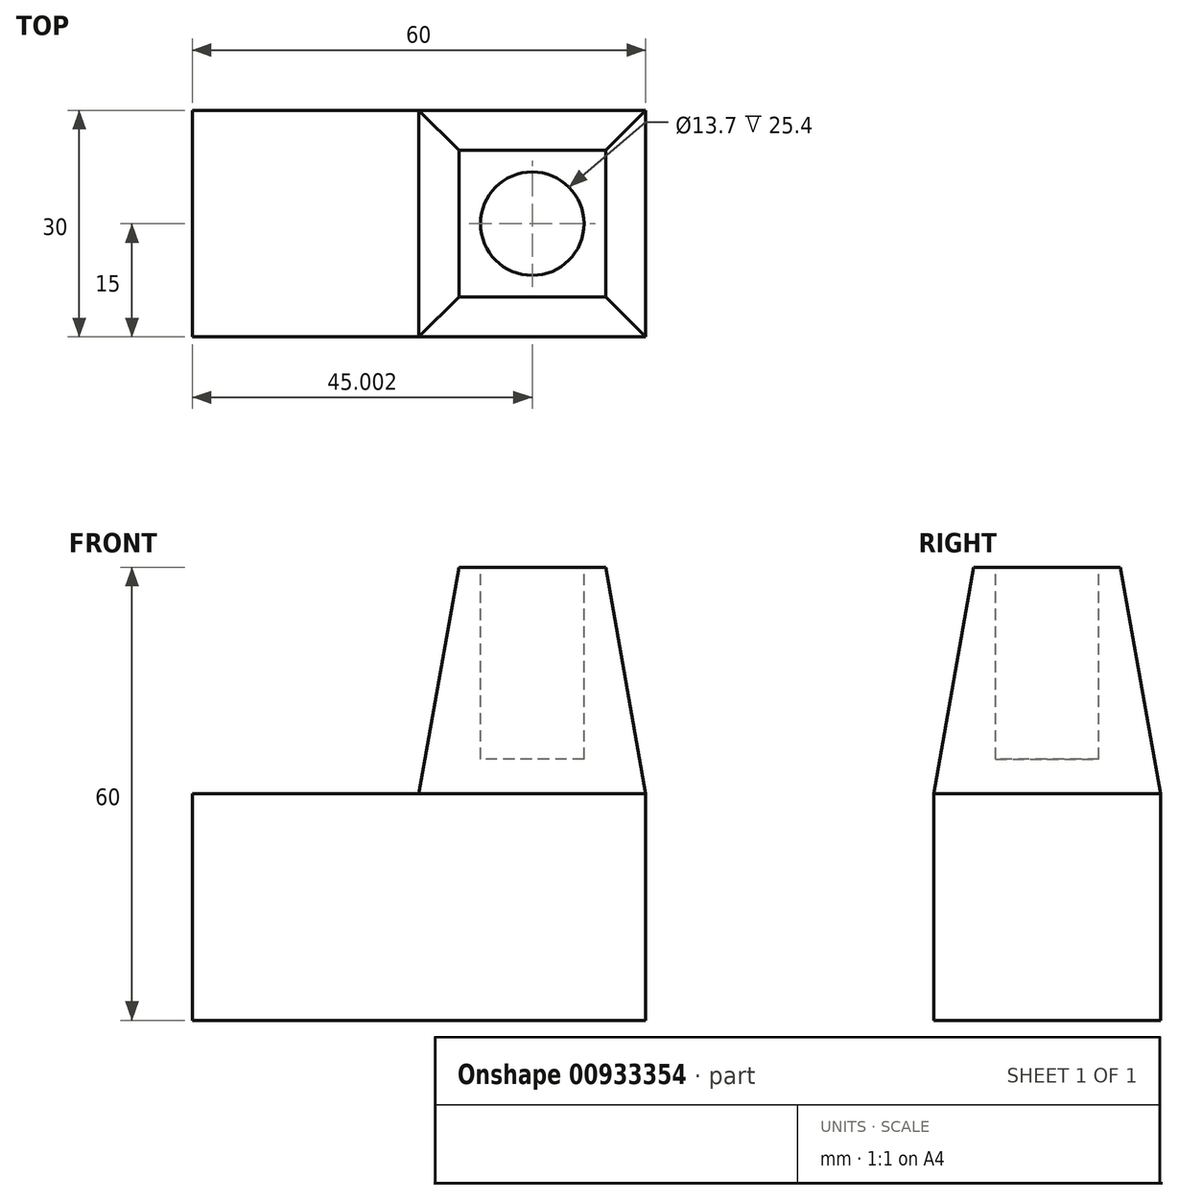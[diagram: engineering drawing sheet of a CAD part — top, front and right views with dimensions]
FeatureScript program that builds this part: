
annotation { "Feature Type Name" : "Feature", "Feature Type Description" : "" }
export const myFeature = defineFeature(function(context is Context, id is Id, definition is map)
    precondition{}
    {
        {
            var Q0;
            Q0=qCreatedBy(makeId("Front.planeOp"),FACE);
            var sketch = newSketch(context, id + "F0", { "sketchPlane" : qUnion([Q0])});
            skLineSegment(sketch, "E0.bottom", {"start": v(-29.57, 15.46) * mm, "end": v(30.43, 15.46) * mm});
            skLineSegment(sketch, "E0.top", {"start": v(-29.57, -14.54) * mm, "end": v(30.43, -14.54) * mm});
            skLineSegment(sketch, "E0.left", {"start": v(-29.57, 15.46) * mm, "end": v(-29.57, -14.54) * mm});
            skLineSegment(sketch, "E0.right", {"start": v(30.43, 15.46) * mm, "end": v(30.43, -14.54) * mm});
            skSolve(sketch);
        }
        {
            var Q0;
            Q0=makeQuery(id+"F0.imprint","IMPRINT",FACE,{"disambiguationData":[TD([[makeQuery(id+"F0.imprint","IMPRINT",EDGE,{"derivedFrom":sQuery(id+"F0.wireOp",EDGE,"E0.bottom")}),-1.0]])]});
            extrude(context, id + "F1", {"entities" : qUnion([Q0]), "depth" : 30 * mm, "offsetDistance" : 25.4 * mm});
        }
        {
            var Q0;
            Q0=makeQuery(id+"F1.opExtrude","SWEPT_FACE",FACE,{"disambiguationData":[OSD([sQuery(id+"F0.wireOp",EDGE,"E0.bottom")])]});
            var sketch = newSketch(context, id + "F2", { "sketchPlane" : qUnion([Q0])});
            skLineSegment(sketch, "E1.bottom", {"start": v(30.43, 0) * mm, "end": v(0.43, 0) * mm});
            skLineSegment(sketch, "E1.top", {"start": v(30.43, -30) * mm, "end": v(0.43, -30) * mm});
            skLineSegment(sketch, "E1.left", {"start": v(30.43, 0) * mm, "end": v(30.43, -30) * mm});
            skLineSegment(sketch, "E1.right", {"start": v(0.43, 0) * mm, "end": v(0.43, -30) * mm});
            skSolve(sketch);
        }
        {
            var Q0;
            Q0=makeQuery(id+"F2.imprint","IMPRINT",FACE,{"disambiguationData":[TD([[makeQuery(id+"F2.imprint","IMPRINT",EDGE,{"derivedFrom":sQuery(id+"F2.wireOp",EDGE,"E1.bottom")}),-1.0]])]});
            extrude(context, id + "F3", {"entities" : qUnion([Q0]), "operationType" : NewBodyOperationType.ADD, "depth" : 30 * mm, "offsetDistance" : 25.4 * mm, "hasDraft" : true, "draftAngle" : 10 * degree, "draftPullDirection" : true});
        }
        {
            var Q0;
            Q0=makeQuery(id+"F3.opExtrude","CAP_FACE",FACE,{"disambiguationData":[OSD([sQuery(id+"F2.wireOp",EDGE,"E1.bottom"),sQuery(id+"F2.wireOp",EDGE,"E1.top"),sQuery(id+"F2.wireOp",EDGE,"E1.left"),sQuery(id+"F2.wireOp",EDGE,"E1.right")])],"isStart":false});
            var sketch = newSketch(context, id + "F4", { "sketchPlane" : qUnion([Q0])});
            skCircle(sketch, "E2", {"center": v(15.43, -15) * mm, "radius": 6.85 * mm});
            skPoint(sketch, "E2.centerSnap0", {"position": v(15.43, -5.29) * mm});
            skPoint(sketch, "E2.centerSnap1", {"position": v(5.72, -15) * mm});
            skSolve(sketch);
        }
        {
            var Q0;
            Q0 = qSketchRegion(id + "F4", true);
            extrude(context, id + "F5", {"entities" : qUnion([Q0]), "operationType" : NewBodyOperationType.REMOVE, "oppositeDirection" : true, "depth" : 25.4 * mm, "offsetDistance" : 25.4 * mm});
        }
    });
